# Revit family: round-tapered-fluted-column-bim
name_source: partatom
category: Columns
units: mm (PartAtom-declared; Revit-internal decimal feet)

## family parameters
Automatically joins geometry to walls = Yes
Classification Number = 23.25.30.11.14.11
Cut with Voids When Loaded = No
Shared = No
Show family pre-cut in plan views = Yes

## types (11) — shared parameters
Assembly Code = 066000
Description = Load-bearing or decorative composite column with Tuscan, Doric, or Attic cap/base, available in Cast Fiberglass, Lightweight Fiberglass, Synthetic Stone, or GFRC.
Manufacturer = Royal Corinthian
Material = RoyalStone Cream
Model = Round Tapered Fluted Column
Product Line = RoyalCast / RoyaLite / RoyalStone / RoyalGFRC
URL = https://royalcorinthian.com

## per-type parameters (varying)
| type | Attic Base _Width | B_Width | D_Height | Doric Base_Width | Doric Cap_Width | T_Height | T_Width | Tuscan Base_Width | Tuscan Cap_Width | Width |
| Round Tapered Fluted Column 8" | 0' - 5" | 0' - 0 1/2" | 0' - 5" | 0' - 3" | 0' - 5 1/2" | 0' - 4 1/2" | 0' - 0 1/2" | 0' - 4 1/2" | 0' - 4 1/2" | 0' - 8" |
| Round Tapered Fluted Column 10" | 0' - 6" | 0' - 1" | 0' - 6 1/2" | 0' - 4" | 0' - 6 1/2" | 0' - 5 1/2" | 0' - 0 1/2" | 0' - 5 1/2" | 0' - 5 1/2" | 0' - 10" |
| Round Tapered Fluted Column 12" | 0' - 7 1/2" | 0' - 1" | 0' - 8" | 0' - 4 1/2" | 0' - 8" | 0' - 6 1/2" | 0' - 1" | 0' - 6 1/2" | 0' - 6 1/2" | 1' - 0" |
| Round Tapered Fluted Column 14" | 0' - 8 1/2" | 0' - 1" | 0' - 9" | 0' - 5 1/2" | 0' - 9" | 0' - 7 1/2" | 0' - 1" | 0' - 7 1/2" | 0' - 7 1/2" | 1' - 2" |
| Round Tapered Fluted Column 16" | 0' - 10" | 0' - 1 1/2" | 0' - 10 1/2" | 0' - 6 1/2" | 0' - 10 1/2" | 0' - 9" | 0' - 1" | 0' - 8 1/2" | 0' - 8 1/2" | 1' - 4" |
| Round Tapered Fluted Column 18" | 0' - 11" | 0' - 1 1/2" | 0' - 11 1/2" | 0' - 7" | 1' - 0" | 0' - 10" | 0' - 1 1/2" | 0' - 10" | 0' - 10" | 1' - 6" |
| Round Tapered Fluted Column 20" | 1' - 0" | 0' - 1 1/2" | 1' - 1" | 0' - 8" | 1' - 1" | 0' - 11" | 0' - 1 1/2" | 0' - 11" | 0' - 11" | 1' - 8" |
| Round Tapered Fluted Column 24" | 1' - 2 1/2" | 0' - 2" | 1' - 3 1/2" | 0' - 9 1/2" | 1' - 4" | 1' - 1" | 0' - 1 1/2" | 1' - 1" | 1' - 1" | 2' - 0" |
| Round Tapered Fluted Column 30" | 1' - 6 1/2" | 0' - 2 1/2" | 1' - 7 1/2" | 1' - 0" | 1' - 7 1/2" | 1' - 4 1/2" | 0' - 2" | 1' - 4 1/2" | 1' - 4 1/2" | 2' - 6" |
| Round Tapered Fluted Column 36" | 1' - 10" | 0' - 3" | 1' - 11 1/2" | 1' - 2" | 1' - 11 1/2" | 1' - 8" | 0' - 2 1/2" | 1' - 7 1/2" | 1' - 7 1/2" | 3' - 0" |
| Round Tapered Fluted Column 48" | 2' - 5 1/2" | 0' - 4" | 2' - 7" | 1' - 7" | 2' - 7 1/2" | 2' - 2 1/2" | 0' - 3 1/2" | 2' - 2" | 2' - 2" | 4' - 0" |

## geometry (parser evidence)
native form markers: Sweep x45
no freeform markers — native parametric forms only
